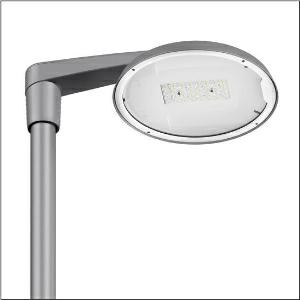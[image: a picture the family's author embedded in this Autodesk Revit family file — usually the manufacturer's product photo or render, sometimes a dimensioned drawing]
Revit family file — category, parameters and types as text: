
# Revit family: dl_50_iq_mini___st0_5a_5xa248b31f08ke_1c6c
name_source: partatom
category: Lighting Fixtures
units: mm (PartAtom-declared; Revit-internal decimal feet)

## family parameters
Cut with Voids When Loaded = No
Host = Face
Light Source = No
Part Type = Normal
Room Calculation Point = No
Round Connector Dimension = Use Diameter
Shared = No

## types (1)
- --- (1 x LED, 5500 lm, 32.1 W, 3000K)
    Apparent Load = 32 VA
    CIE Flux Codes = 43 76 97 100 100
    Color Rendering = 70
    Color Temperature = 3000K
    Default Elevation = 1800 mm
    Description = DL 50 iQ mini, mast luminaire, primary light control with lens, of PMMA, primary optical cover: cover, of toughened safety glass, transparent, light distribution: ST0.5a, light emission: direct distribution, primary light characteristic: asymmetric, installation type: side-entry, post-top, LED, High Power LED, rated luminous flux: 5.500lm, luminous efficacy: 171lm/W, light colour: 730, colour temperature: 3000K, control gear: iQ Street-Remote, control: optimised constant luminous flux control (CLO 2.0), Desk-Remote (wireless, voltage-free reading and setting of iQ features in the workshop via application-optimized NFC function/RFID function), Light-Fading, Smart-Wire, Night-Set, Lumen-Switch, Temp-Guard, Auto-Match, Street-Remote, mains connection: 230..240V, AC, 50/60Hz, connection cable pre-assembled, cable length: 6,5m, start of lifetime: 32W, end of service life: 33W, reduction: 16W, luminaire housing, of diecast aluminium, powder-coated, SITECO metallic grey (DB 702S), inclination adjustable: 0°, 5°, 10° (post-top) | 0°, -5°, -10°, -15° (side-entry), please order mast post-top element or mast side-entry element separately, diameter: 500mm, height: 115mm, post-top: for spigot size d x l = 76 x 100mm; with reducer (optional accessory) 60 x 100mm | side-entry: for spigot size d x l = 60 x 100mm; with reducer (optional accessory) 42 x 100mm, mounting height: 4..6m, protection rating (complete): IP66, insulation class (complete): insulation class II (safety insulation), certification: CE, ENEC, ENEC+, VDE, impact resistance: IK08, permissible operating ambient temperature for outdoor applications: -25..+40°C, standard-compliant lighting for roads and squares, packaging unit: 1 piece

Light Distribution: ST0.5a
    Height = 115 mm
    Lamp = 1 x LED
    Lamp Light Flux = 5500 lm
    Lamp Power = 32.1 W
    Lamp count = 1
    Length = 500 mm
    Luminous efficacy = 171 lm/W
    Manufacturer = Siteco
    ModVariant = No
    Model = 5XA248B31F08KE
    Mounting Place = Pole
    Mounting Type = Pole top
    Number of Poles = 1
    OnlyDefault = Yes
    Power Factor = 1
    Product Name = DL 50 iQ mini | ST0.5a
    Product group = mast luminaire | pylon top
    ProductGroupID = 6100
    Protection Class = Protection class II
    Protection Degree = IP 66
    RLX_Detail_Level = 1
    RLX_Emergency_Light_Flux = 0 lm
    RLX_Emergency_Type = 0
    RLX_Emergency_Type_DB = No
    RlxData = <blob elided: 127073 chars, md5=90bc2224>
    Socket = socket
    Standby Power = 0 W
    System Light Flux = 5500 lm
    System Power = 32 W
    Type Comments = factory setting: luminous flux: 100 % | dim-lin: 254 | 343 mA
    Type Image = l_1251794.jpg
    URL = http://relux.com
    VarID = @adj_144047
    Voltage = 0 V
    Weight = 0.00 kg
    Width = 0 mm  [stored 0 ft]

note: [stored X ft] marks values corroborated as IEEE doubles in the binary element streams (Revit-internal decimal feet)

## geometry (parser evidence)
native form markers: Blend x4, Sweep x12
no freeform markers — native parametric forms only
